# Revit family: Toilet-Floor_Mount-KOHLER-MODERN_LIFE-K-78846H_1
name_source: partatom
category: Plumbing Fixtures
revit_build: Autodesk Revit 2017 (Build: 20160225_1515(x64)
units: mm (PartAtom-declared; Revit-internal decimal feet)

## family parameters
Cut with Voids When Loaded = No
Host = Face
OmniClass Number = 23.31.19.00
OmniClass Title = Toilets
Part Type = Normal
Room Calculation Point = No
Round Connector Dimension = Use Diameter
Shared = No

## types (2) — shared parameters
ADA Compliant = No
Assembly Code = D2010100
Bowl Height = 16 1/8"
CW Connection = Yes
Cold Water Inlet = Cold Water Inlet
Date Modified = 08/06/2021
Default Elevation = 0"
Finish = Kohler-Vitreous_China-0-White
Flow Rate = 0 GPM
Flush Rate- GPF = 0 GPF
Flush Rate- LPF = 0 LPF
HW Connection = No
Hot Water Inlet = Hot Water Inlet
Length = 25 3/4"
Manufacturer = KOHLER Co.
Master Format 2014 = 22 42 13.13
Master Format 2014 Name = Residential Water Closets
Material = Vitreous China
Pressure = 0.00 psi
Product Documentation Link = http://resources.kohler.com
Product Name = Modern Life
Product Page URL = https://www.kohlerasiapacific.com
Rough-In = 8 7/8"
Seat Included = Yes
URL = https://www.kohlerasiapacific.com
Vent Connection = No
Waste Connection = Yes
Waste Water Outlet = Waste Water Outlet
WaterSense Certified = No
Width = 15 1/2"

## per-type parameters (varying)
| type | Description | Height | K-78846H | Model | Touchless | Type |
| 0-White | Close-Coupled Dual Flush 3/6L Washdown Toilet with Rimless Flushing Technology and Slim Seat Ceramic S-trap | 31 1/8" | Yes | K-78846H-0 | No | 1 |
| Touchless, 0-White | 2PC WD BTW | 30 15/16" | No | K-78846H-TF-0 | Yes | 2 |

## geometry (parser evidence)
native form markers: Sweep x3
no freeform markers — native parametric forms only
